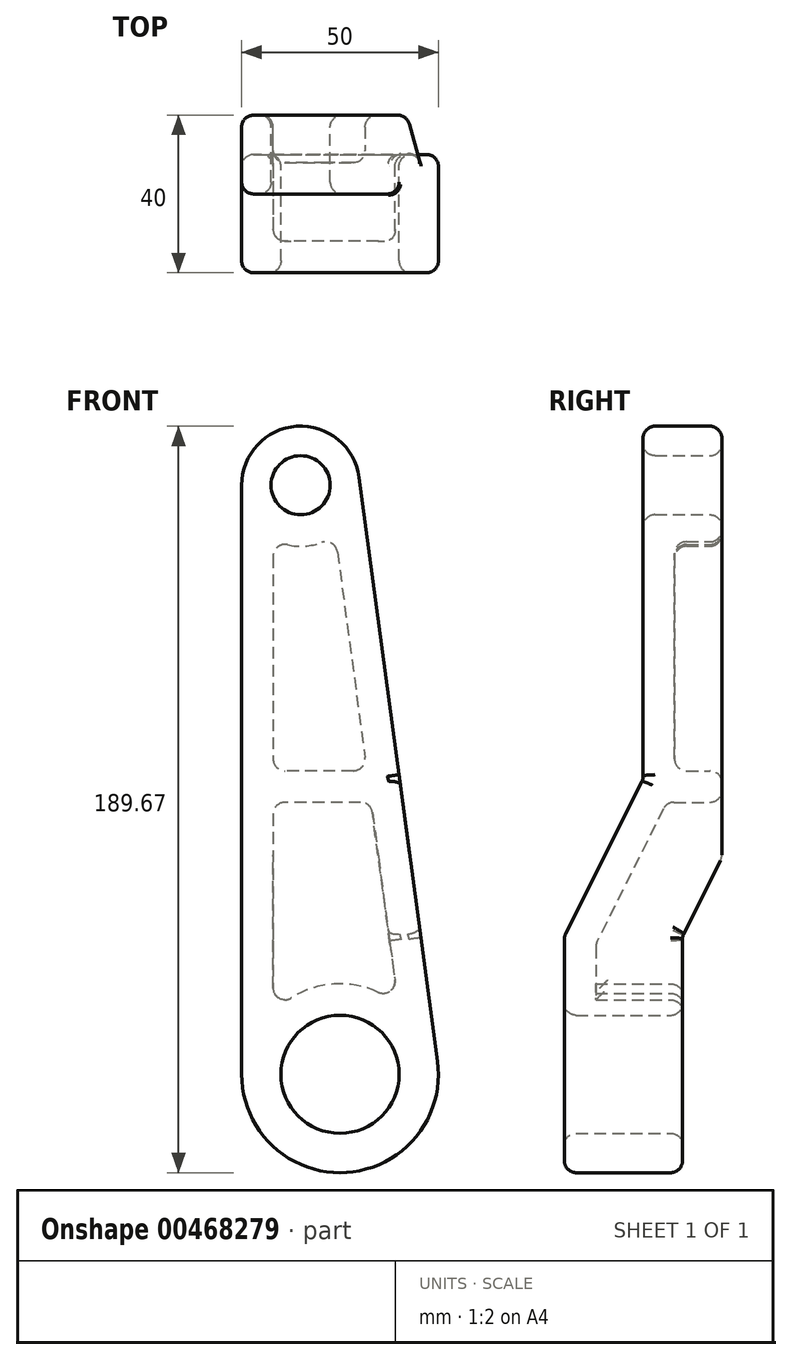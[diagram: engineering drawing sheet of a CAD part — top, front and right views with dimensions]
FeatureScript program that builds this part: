
annotation { "Feature Type Name" : "Feature", "Feature Type Description" : "" }
export const myFeature = defineFeature(function(context is Context, id is Id, definition is map)
    precondition{}
    {
        {
            var Q0;
            Q0=qCreatedBy(makeId("Front.planeOp"),FACE);
            var sketch = newSketch(context, id + "F0", { "sketchPlane" : qUnion([Q0])});
            skArc(sketch, "E0", {"start": v(-25, 0) * mm, "mid": v(1.67, -24.94) * mm, "end": v(24.78, 3.33) * mm});
            skArc(sketch, "E1", {"start": v(4.87, 151.66) * mm, "mid": v(-11, 164.63) * mm, "end": v(-25, 149.67) * mm});
            skLineSegment(sketch, "E2", {"start": v(-25, 149.67) * mm, "end": v(-25, 0) * mm});
            skLineSegment(sketch, "E3", {"start": v(4.87, 151.66) * mm, "end": v(24.78, 3.33) * mm});
            skSolve(sketch);
        }
        {
            var Q0;
            Q0=makeQuery(id+"F0.imprint","IMPRINT",FACE,{"disambiguationData":[TD([[makeQuery(id+"F0.imprint","IMPRINT",EDGE,{"derivedFrom":sQuery(id+"F0.wireOp",EDGE,"E0")}),1.0]])]});
            extrude(context, id + "F1", {"entities" : qUnion([Q0]), "depth" : 40 * mm});
        }
        {
            var Q0;
            Q0=makeQuery(id+"F1.opExtrude","SWEPT_FACE",FACE,{"disambiguationData":[OSD([sQuery(id+"F0.wireOp",EDGE,"E2")])]});
            var sketch = newSketch(context, id + "F2", { "sketchPlane" : qUnion([Q0])});
            skLineSegment(sketch, "E4", {"start": v(0, 0) * mm, "end": v(0, -25.94) * mm});
            skLineSegment(sketch, "E5", {"start": v(0, -25.94) * mm, "end": v(10, -25.94) * mm});
            skLineSegment(sketch, "E6", {"start": v(10, -25.94) * mm, "end": v(10, 35) * mm});
            skLineSegment(sketch, "E7", {"start": v(10, 35) * mm, "end": v(0, 55) * mm});
            skLineSegment(sketch, "E8", {"start": v(0, 55) * mm, "end": v(0, 0) * mm});
            skLineSegment(sketch, "E9", {"start": v(40, 35) * mm, "end": v(40, 149.67) * mm});
            skLineSegment(sketch, "E10", {"start": v(40, 149.67) * mm, "end": v(40, 165.63) * mm});
            skLineSegment(sketch, "E11", {"start": v(40, 165.63) * mm, "end": v(20, 165.63) * mm});
            skLineSegment(sketch, "E12", {"start": v(20, 165.63) * mm, "end": v(20, 75) * mm});
            skLineSegment(sketch, "E13", {"start": v(20, 75) * mm, "end": v(40, 35) * mm});
            skSolve(sketch);
        }
        {
            var Q0;
            {var subQ0=sQuery(id+"F2.wireOp",EDGE,"E9");Q0=makeQuery(id+"F2.imprint","IMPRINT",FACE,{"disambiguationData":[TD([[makeQuery(id+"F2.imprint","IMPRINT",EDGE,{"derivedFrom":subQ0}),-1.0]])]});}
            var Q1;
            {var subQ0=sQuery(id+"F2.wireOp",EDGE,"E10");Q1=makeQuery(id+"F2.imprint","IMPRINT",FACE,{"disambiguationData":[TD([[makeQuery(id+"F2.imprint","IMPRINT",EDGE,{"derivedFrom":subQ0}),1.0]])]});}
            var Q2;
            {var subQ0=sQuery(id+"F2.wireOp",EDGE,"E7");Q2=makeQuery(id+"F2.imprint","IMPRINT",FACE,{"disambiguationData":[TD([[makeQuery(id+"F2.imprint","IMPRINT",EDGE,{"derivedFrom":subQ0}),1.0]])]});}
            var Q3;
            {var subQ0=sQuery(id+"F2.wireOp",EDGE,"E4");Q3=makeQuery(id+"F2.imprint","IMPRINT",FACE,{"disambiguationData":[TD([[makeQuery(id+"F2.imprint","IMPRINT",EDGE,{"derivedFrom":subQ0}),1.0]])]});}
            extrude(context, id + "F3", {"entities" : qUnion([Q0, Q1, Q2, Q3]), "operationType" : NewBodyOperationType.REMOVE, "endBound" : BoundingType.THROUGH_ALL, "oppositeDirection" : true, "depth" : 25 * mm});
        }
        {
            var Q0;
            Q0=makeQuery(id+"F1.opExtrude","CAP_FACE",FACE,{"disambiguationData":[OSD([sQuery(id+"F0.wireOp",EDGE,"E0"),sQuery(id+"F0.wireOp",EDGE,"E1"),sQuery(id+"F0.wireOp",EDGE,"E2"),sQuery(id+"F0.wireOp",EDGE,"E3")])],"isStart":true});
            var sketch = newSketch(context, id + "F4", { "sketchPlane" : qUnion([Q0])});
            skCircle(sketch, "E14", {"center": v(10, 149.67) * mm, "radius": 7.5 * mm});
            skCircle(sketch, "E15", {"center": v(0, 0) * mm, "radius": 15 * mm});
            skSolve(sketch);
        }
        {
            var Q0;
            Q0=qSketchRegion(id+"F4",true);
            extrude(context, id + "F5", {"entities" : qUnion([Q0]), "operationType" : NewBodyOperationType.REMOVE, "endBound" : BoundingType.THROUGH_ALL, "oppositeDirection" : true, "depth" : 25 * mm});
        }
        {
            var Q0;
            Q0=makeQuery(id+"F1.opExtrude","CAP_FACE",FACE,{"disambiguationData":[OSD([sQuery(id+"F0.wireOp",EDGE,"E0"),sQuery(id+"F0.wireOp",EDGE,"E1"),sQuery(id+"F0.wireOp",EDGE,"E2"),sQuery(id+"F0.wireOp",EDGE,"E3")])],"isStart":true});
            var Q1;
            Q1=makeQuery(id+"F3.boolean.opBoolean","COPY",FACE,{"derivedFrom":makeQuery(id+"F3.opExtrude","SWEPT_FACE",FACE,{"disambiguationData":[OSD([sQuery(id+"F2.wireOp",EDGE,"E7")])]})});
            var Q2;
            Q2=makeQuery(id+"F3.boolean.opBoolean","COPY",FACE,{"derivedFrom":makeQuery(id+"F3.opExtrude","SWEPT_FACE",FACE,{"disambiguationData":[OSD([sQuery(id+"F2.wireOp",EDGE,"E6")])]})});
            shell(context, id + "F6", {"entities" : qUnion([Q0, Q1, Q2]), "thickness" : 8 * mm});
        }
        {
            var Q0;
            Q0=makeQuery(id+"F1.opExtrude","CAP_FACE",FACE,{"disambiguationData":[OSD([sQuery(id+"F0.wireOp",EDGE,"E0"),sQuery(id+"F0.wireOp",EDGE,"E1"),sQuery(id+"F0.wireOp",EDGE,"E2"),sQuery(id+"F0.wireOp",EDGE,"E3")])],"isStart":true});
            var sketch = newSketch(context, id + "F7", { "sketchPlane" : qUnion([Q0])});
            skLineSegment(sketch, "E16", {"start": v(-6.8, 77.11) * mm, "end": v(17, 77.11) * mm});
            skLineSegment(sketch, "E17", {"start": v(-7.88, 69.11) * mm, "end": v(17, 69.11) * mm});
            skSolve(sketch);
        }
        {
            var Q0;
            {var subQ0=sQuery(id+"F7.wireOp",EDGE,"E16");Q0=makeQuery(id+"F7.imprint","IMPRINT",FACE,{"disambiguationData":[TD([[makeQuery(id+"F7.imprint","IMPRINT",EDGE,{"derivedFrom":subQ0}),-1.0]])]});}
            var Q1;
            Q1=makeQuery(id+"F1.opExtrude","SWEPT_BODY",BODY,{"disambiguationData":[OSD([sQuery(id+"F0.wireOp",EDGE,"E0"),sQuery(id+"F0.wireOp",EDGE,"E1"),sQuery(id+"F0.wireOp",EDGE,"E2"),sQuery(id+"F0.wireOp",EDGE,"E3")])]});
            extrude(context, id + "F8", {"entities" : qUnion([Q0]), "operationType" : NewBodyOperationType.ADD, "endBound" : BoundingType.UP_TO_NEXT, "oppositeDirection" : true, "endBoundEntityBody" : qUnion([Q1]), "depth" : 4 * mm});
        }
        {
            var Q0;
            Q0=makeQuery(id+"F6.opShell","OFFSET_FACE",FACE,{"disambiguationData":[OSD([sQuery(id+"F2.wireOp",EDGE,"E7")])]});
            var Q1;
            Q1=makeQuery(id+"F3.boolean.opBoolean","COPY",FACE,{"derivedFrom":makeQuery(id+"F3.opExtrude","SWEPT_FACE",FACE,{"disambiguationData":[OSD([sQuery(id+"F2.wireOp",EDGE,"E7")])]})});
            var Q2;
            Q2=makeQuery(id+"F6.opShell","OFFSET_FACE",FACE,{"disambiguationData":[OSD([sQuery(id+"F2.wireOp",EDGE,"E13")])]});
            var Q3;
            {var subQ1=sQuery(id+"F0.wireOp",EDGE,"E2");Q3=makeQuery(id+"F8.boolean.opBoolean","SPLIT",FACE,{"disambiguationData":[TD([makeQuery(id+"F3.boolean.opBoolean","COPY",FACE,{"derivedFrom":makeQuery(id+"F3.opExtrude","SWEPT_FACE",FACE,{"disambiguationData":[OSD([sQuery(id+"F2.wireOp",EDGE,"E6")])]})})])],"derivedFrom":makeQuery(id+"F6.opShell","OFFSET_FACE",FACE,{"disambiguationData":[OSD([subQ1])]})});}
            var Q4;
            {var subQ0=sQuery(id+"F0.wireOp",EDGE,"E3");Q4=makeQuery(id+"F8.boolean.opBoolean","SPLIT",FACE,{"disambiguationData":[TD([makeQuery(id+"F3.boolean.opBoolean","COPY",FACE,{"derivedFrom":makeQuery(id+"F3.opExtrude","SWEPT_FACE",FACE,{"disambiguationData":[OSD([sQuery(id+"F2.wireOp",EDGE,"E6")])]})})])],"derivedFrom":makeQuery(id+"F6.opShell","OFFSET_FACE",FACE,{"disambiguationData":[OSD([subQ0])]})});}
            var Q5;
            Q5=makeQuery(id+"F3.boolean.opBoolean","COPY",FACE,{"derivedFrom":makeQuery(id+"F3.opExtrude","SWEPT_FACE",FACE,{"disambiguationData":[OSD([sQuery(id+"F2.wireOp",EDGE,"E6")])]})});
            var Q6;
            Q6=makeQuery(id+"F3.boolean.opBoolean","COPY",FACE,{"derivedFrom":makeQuery(id+"F3.opExtrude","SWEPT_FACE",FACE,{"disambiguationData":[OSD([sQuery(id+"F2.wireOp",EDGE,"E13")])]})});
            var Q7;
            Q7=makeQuery(id+"F1.opExtrude","CAP_FACE",FACE,{"disambiguationData":[OSD([sQuery(id+"F0.wireOp",EDGE,"E0"),sQuery(id+"F0.wireOp",EDGE,"E1"),sQuery(id+"F0.wireOp",EDGE,"E2"),sQuery(id+"F0.wireOp",EDGE,"E3")])],"isStart":false});
            var Q8;
            {var subQ1=sQuery(id+"F0.wireOp",EDGE,"E3");Q8=makeQuery(id+"F8.boolean.opBoolean","SPLIT",FACE,{"disambiguationData":[TD([makeQuery(id+"F6.opShell","OFFSET_FACE",FACE,{"disambiguationData":[OSD([sQuery(id+"F4.wireOp",EDGE,"E14")])]})])],"derivedFrom":makeQuery(id+"F6.opShell","OFFSET_FACE",FACE,{"disambiguationData":[OSD([subQ1])]})});}
            var Q9;
            Q9=makeQuery(id+"F3.boolean.opBoolean","COPY",FACE,{"derivedFrom":makeQuery(id+"F3.opExtrude","SWEPT_FACE",FACE,{"disambiguationData":[OSD([sQuery(id+"F2.wireOp",EDGE,"E12")])]})});
            var Q10;
            Q10=makeQuery(id+"F5.boolean.opBoolean","COPY",FACE,{"derivedFrom":makeQuery(id+"F5.opExtrude","SWEPT_FACE",FACE,{"disambiguationData":[OSD([sQuery(id+"F4.wireOp",EDGE,"E14")])]})});
            var Q11;
            Q11=makeQuery(id+"F6.opShell","OFFSET_FACE",FACE,{"disambiguationData":[OSD([sQuery(id+"F2.wireOp",EDGE,"E12")])]});
            var Q12;
            Q12=makeQuery(id+"F6.opShell","OFFSET_FACE",FACE,{"disambiguationData":[OSD([sQuery(id+"F4.wireOp",EDGE,"E14")])]});
            var Q13;
            Q13=makeQuery(id+"F8.opExtrude","CAP_EDGE",EDGE,{"disambiguationData":[OSD([sQuery(id+"F7.wireOp",EDGE,"E16")])],"isStart":true});
            var Q14;
            Q14=makeQuery(id+"F1.opExtrude","SWEPT_FACE",FACE,{"disambiguationData":[OSD([sQuery(id+"F0.wireOp",EDGE,"E3")])]});
            var Q15;
            Q15=makeQuery(id+"F1.opExtrude","CAP_EDGE",EDGE,{"disambiguationData":[OSD([sQuery(id+"F0.wireOp",EDGE,"E3")])],"isStart":true});
            var Q16;
            {var subQ0=sQuery(id+"F0.wireOp",EDGE,"E2");Q16=makeQuery(id+"F8.boolean.opBoolean","SPLIT",EDGE,{"disambiguationData":[TD([makeQuery(id+"F3.boolean.opBoolean","COPY",FACE,{"derivedFrom":makeQuery(id+"F3.opExtrude","SWEPT_FACE",FACE,{"disambiguationData":[OSD([sQuery(id+"F2.wireOp",EDGE,"E7")])]})})])],"derivedFrom":makeQuery(id+"F6.opShell","OFFSET_EDGE",EDGE,{"disambiguationData":[OSD([subQ0]),TDD([makeQuery(id+"F1.opExtrude","CAP_EDGE",EDGE,{"disambiguationData":[OSD([subQ0])],"isStart":true})])]})});}
            var Q17;
            Q17=makeQuery(id+"F1.opExtrude","CAP_EDGE",EDGE,{"disambiguationData":[OSD([sQuery(id+"F0.wireOp",EDGE,"E2")])],"isStart":true});
            var Q18;
            Q18=makeQuery(id+"F8.opExtrude","CAP_EDGE",EDGE,{"disambiguationData":[OSD([sQuery(id+"F7.wireOp",EDGE,"E17")])],"isStart":true});
            var Q19;
            {var subQ2=sQuery(id+"F0.wireOp",EDGE,"E2");Q19=makeQuery(id+"F8.boolean.opBoolean","SPLIT",EDGE,{"disambiguationData":[TD([makeQuery(id+"F6.opShell","OFFSET_FACE",FACE,{"disambiguationData":[OSD([sQuery(id+"F4.wireOp",EDGE,"E14")])]})])],"derivedFrom":makeQuery(id+"F6.opShell","OFFSET_EDGE",EDGE,{"disambiguationData":[OSD([subQ2]),TDD([makeQuery(id+"F1.opExtrude","CAP_EDGE",EDGE,{"disambiguationData":[OSD([subQ2])],"isStart":true})])]})});}
            var Q20;
            Q20=makeQuery(id+"F1.opExtrude","CAP_EDGE",EDGE,{"disambiguationData":[OSD([sQuery(id+"F0.wireOp",EDGE,"E1")])],"isStart":true});
            var Q21;
            Q21=makeQuery(id+"F8.opExtrude","SWEPT_EDGE",EDGE,{"disambiguationData":[OSD([sQuery(id+"F0.wireOp",EDGE,"E2"),sQuery(id+"F7.wireOp",EDGE,"E16")])]});
            fillet(context, id + "F9", {"entities" : qUnion([Q0, Q1, Q2, Q3, Q4, Q5, Q6, Q7, Q8, Q9, Q10, Q11, Q12, Q13, Q14, Q15, Q16, Q17, Q18, Q19, Q20, Q21]), "radius" : 3 * mm, "tangentPropagation" : true, "allowEdgeOverflow" : false});
        }
    });
